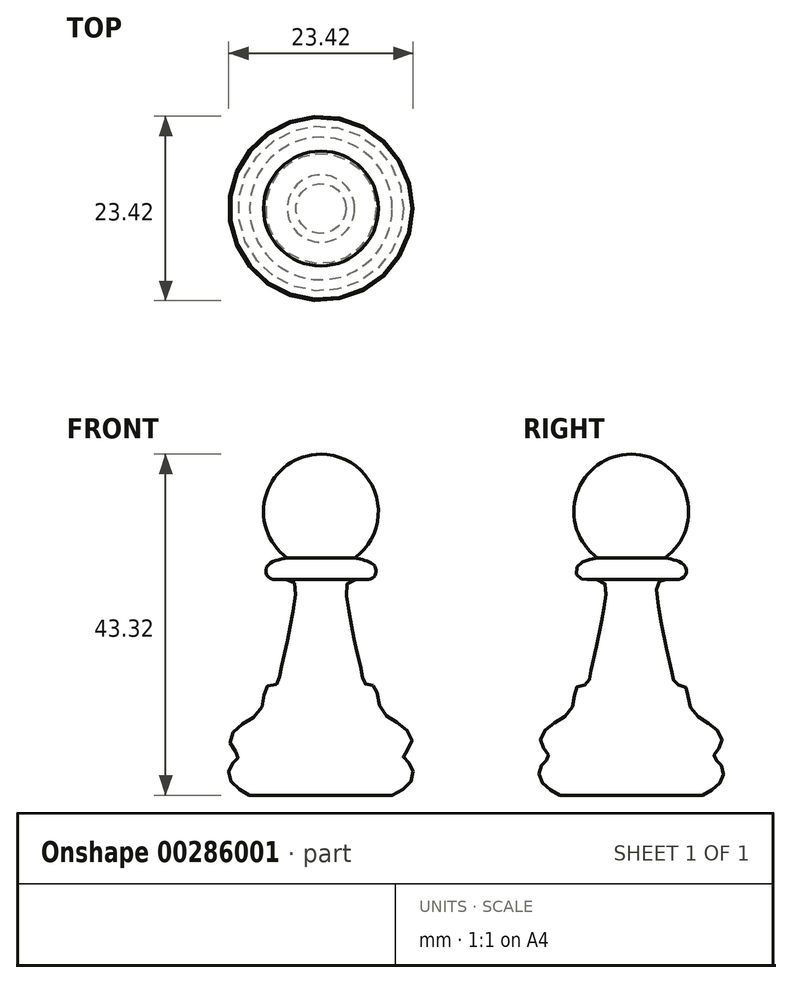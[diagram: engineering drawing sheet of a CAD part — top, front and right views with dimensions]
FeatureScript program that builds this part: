
annotation { "Feature Type Name" : "Feature", "Feature Type Description" : "" }
export const myFeature = defineFeature(function(context is Context, id is Id, definition is map)
    precondition{}
    {
        {
            var Q0;
            Q0=qCreatedBy(makeId("Front.planeOp"),FACE);
            var sketch = newSketch(context, id + "F0", { "sketchPlane" : qUnion([Q0])});
            skLineSegment(sketch, "E0", {"start": v(4.36, -90.5) * mm, "end": v(29.76, -90.5) * mm});
            skArc(sketch, "E1", {"start": v(151.71, -62.22) * mm, "mid": v(154.36, -54.07) * mm, "end": v(147.43, -49.03) * mm});
            skLineSegment(sketch, "E2", {"start": v(147.43, -49.03) * mm, "end": v(147.43, -92.35) * mm});
            skPoint(sketch, "E2.endSnap0", {"position": v(147.43, -62.22) * mm});
            skPoint(sketch, "E3.3.internal.orphan", {"position": v(151.71, -64.76) * mm});
            skPoint(sketch, "E3.5.internal.orphan", {"position": v(151.71, -75.23) * mm});
            skLineSegment(sketch, "E4", {"start": v(147.43, -92.35) * mm, "end": v(156.48, -92.35) * mm});
            skFitSpline(sketch, "E5", {"points": [v(156.48, -92.35) * mm, v(158.86, -90.6) * mm, v(158.86, -88.54) * mm, v(157.9, -87.43) * mm, v(158.93, -85.77) * mm, v(157.75, -83.55) * mm, v(155.05, -81.41) * mm, v(154.25, -78.5) * mm, v(153.07, -78.25) * mm, v(152.6, -76.74) * mm, v(151.71, -72.94) * mm, v(150.94, -68.66) * mm, v(151.02, -65.18) * mm, v(153.95, -64.78) * mm, v(154.26, -63.28) * mm, v(151.71, -62.22) * mm], "startDerivative": vector(40.28, 20.36) * mm, "endDerivative": vector(-46.64, 8.78) * mm});
            skSolve(sketch);
        }
        {
            var Q0;
            Q0=makeQuery(id+"F0.imprint","IMPRINT",FACE,{"disambiguationData":[TD([[makeQuery(id+"F0.imprint","IMPRINT",EDGE,{"derivedFrom":sQuery(id+"F0.wireOp",EDGE,"E1")}),1.0]])]});
            var Q1;
            Q1=sQuery(id+"F0.wireOp",EDGE,"E2");
            revolve(context, id + "F1", {"entities" : qUnion([Q0]), "axis" : qUnion([Q1]), "revolveType" : RevolveType.FULL});
        }
    });
